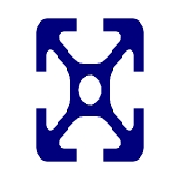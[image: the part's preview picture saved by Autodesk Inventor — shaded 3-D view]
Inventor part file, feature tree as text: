
AUTODESK INVENTOR PART (.ipt)
format: ipt  version: 2020 (Build 240168000, 168)  size: 278,016 bytes
history: native  units: mm
features: other x16, sketch x8, plane x1, split x1
ambient origin geometry x8: Origin, YZ Plane, XZ Plane, XY Plane, X Axis, Y Axis, Z Axis, Center Point
bodies: Body (feature_tree)
feature tree (26):
  other  "Řízená délka"
  other  "Těleso1"
  other  "Start Plane"
  other  "End Plane"
  other  "iFeatureSketch"
  other  "DRAZKA_20:1"
  other  "DRAZKA_20:2"
  other  "DRAZKA_20:3"
  other  "DRAZKA_20:4"
  other  "DIRA_20:1"
  other  "DRAZKA_20:1Axis"
  other  "DRAZKA_20:2Axis"
  other  "DRAZKA_20:3Axis"
  other  "DRAZKA_20:4Axis"
  other  "DIRA_20:1Axis"
  plane  "Work Plane5"
  split  "Split1"
  sketch  "Sketch"  dims[d2=20.0mm d3=20.0mm d4=2.0mm d9=10.0mm d10=100.0mm d11=0.13mm d12=0.0mm d15=0.83mm d16=0.83mm d17=9.8mm d18=3.0mm d19=4.55mm d20=45.0deg d21=5.2mm d22=1.8mm d24=1.0mm d26=0.83mm d27=0.83mm d28=9.8mm d29=3.0mm d30=4.55mm d31=45.0deg d32=5.2mm d33=1.8mm d35=1.0mm d37=0.83mm d38=0.83mm d39=9.8mm d40=3.0mm d41=4.55mm d42=45.0deg d43=5.2mm d44=1.8mm d46=1.0mm d48=0.83mm d49=0.83mm d50=9.8mm d51=3.0mm d52=4.55mm d53=45.0deg d54=5.2mm d55=1.8mm d57=1.0mm d59=4.3mm d60=0.0mm d61=0.0mm d62=0.0mm d63=0.0mm d64=0.0mm d65=0.0mm d66=0.0mm d67=0.0mm d76=90.0deg d14=90.0mm]
  sketch  "Náčrt11"
  other  "Pracovní rovina4"
  sketch  "Náčrt12"
  sketch  "Náčrt6"
  sketch  "Náčrt7"
  sketch  "Náčrt8"
  sketch  "Náčrt9"
  sketch  "Náčrt10"
